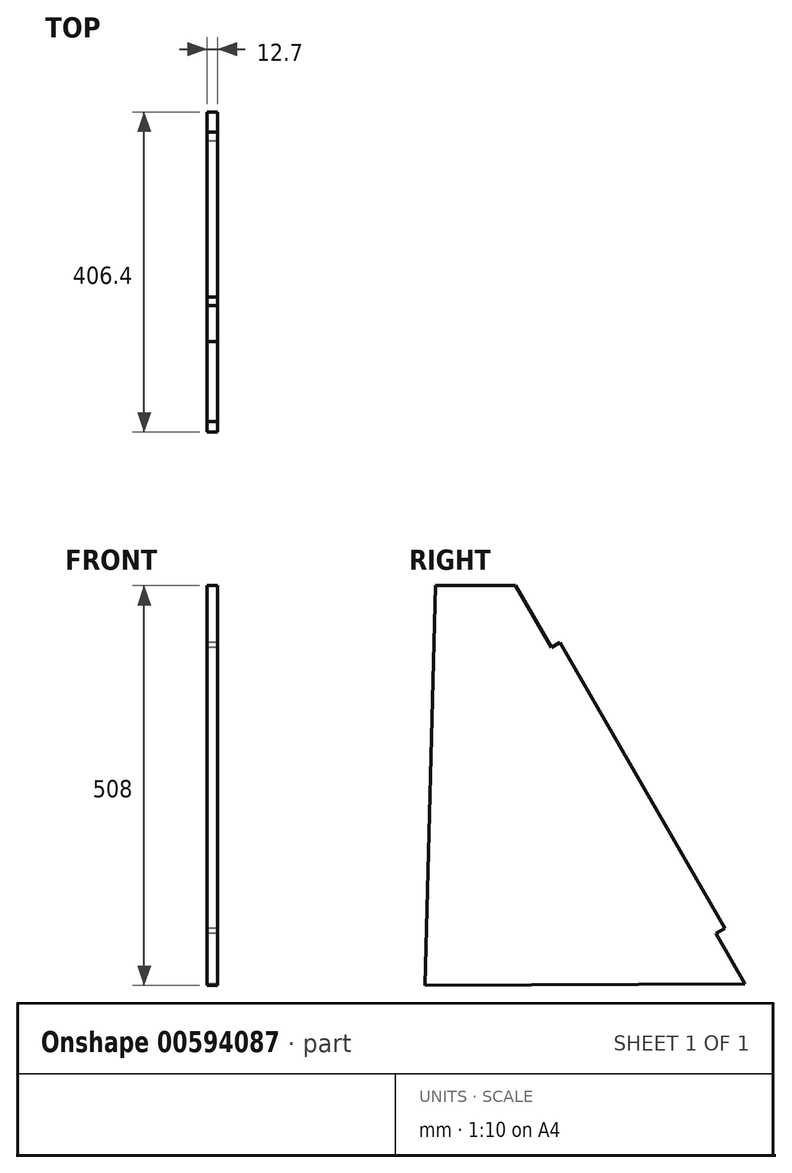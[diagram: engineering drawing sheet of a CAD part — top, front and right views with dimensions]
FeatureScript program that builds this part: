
annotation { "Feature Type Name" : "Feature", "Feature Type Description" : "" }
export const myFeature = defineFeature(function(context is Context, id is Id, definition is map)
    precondition{}
    {
        {
            var Q0;
            Q0=qCreatedBy(makeId("Right.planeOp"),FACE);
            var sketch = newSketch(context, id + "F0", { "sketchPlane" : qUnion([Q0])});
            skLineSegment(sketch, "E0", {"start": v(-8.3, -27.17) * mm, "end": v(5.3, 480.83) * mm});
            skLineSegment(sketch, "E1", {"start": v(5.3, 480.83) * mm, "end": v(106.9, 480.83) * mm});
            skLineSegment(sketch, "E2", {"start": v(106.9, 480.83) * mm, "end": v(398.1, -24.9) * mm});
            skLineSegment(sketch, "E3", {"start": v(398.1, -24.9) * mm, "end": v(-8.3, -27.17) * mm});
            skLineSegment(sketch, "E4", {"start": v(152.35, 401.9) * mm, "end": v(163.36, 408.23) * mm});
            skLineSegment(sketch, "E5", {"start": v(163.36, 408.23) * mm, "end": v(201.38, 342.2) * mm});
            skLineSegment(sketch, "E6", {"start": v(220.4, 309.18) * mm, "end": v(258.42, 243.14) * mm});
            skLineSegment(sketch, "E7", {"start": v(277.43, 210.12) * mm, "end": v(315.45, 144.09) * mm});
            skLineSegment(sketch, "E8", {"start": v(334.46, 111.07) * mm, "end": v(372.48, 45.03) * mm});
            skLineSegment(sketch, "E9", {"start": v(372.48, 45.03) * mm, "end": v(361.48, 38.7) * mm});
            skLineSegment(sketch, "E10", {"start": v(201.38, 342.2) * mm, "end": v(220.4, 309.18) * mm});
            skLineSegment(sketch, "E11", {"start": v(258.42, 243.14) * mm, "end": v(277.43, 210.12) * mm});
            skLineSegment(sketch, "E12", {"start": v(315.45, 144.09) * mm, "end": v(334.46, 111.07) * mm});
            skSolve(sketch);
        }
        {
            var Q0;
            Q0 = qSketchRegion(id + "F0", true);
            extrude(context, id + "F1", {"entities" : qUnion([Q0]), "depth" : 12.7 * mm, "offsetDistance" : 25.4 * mm});
        }
    });
